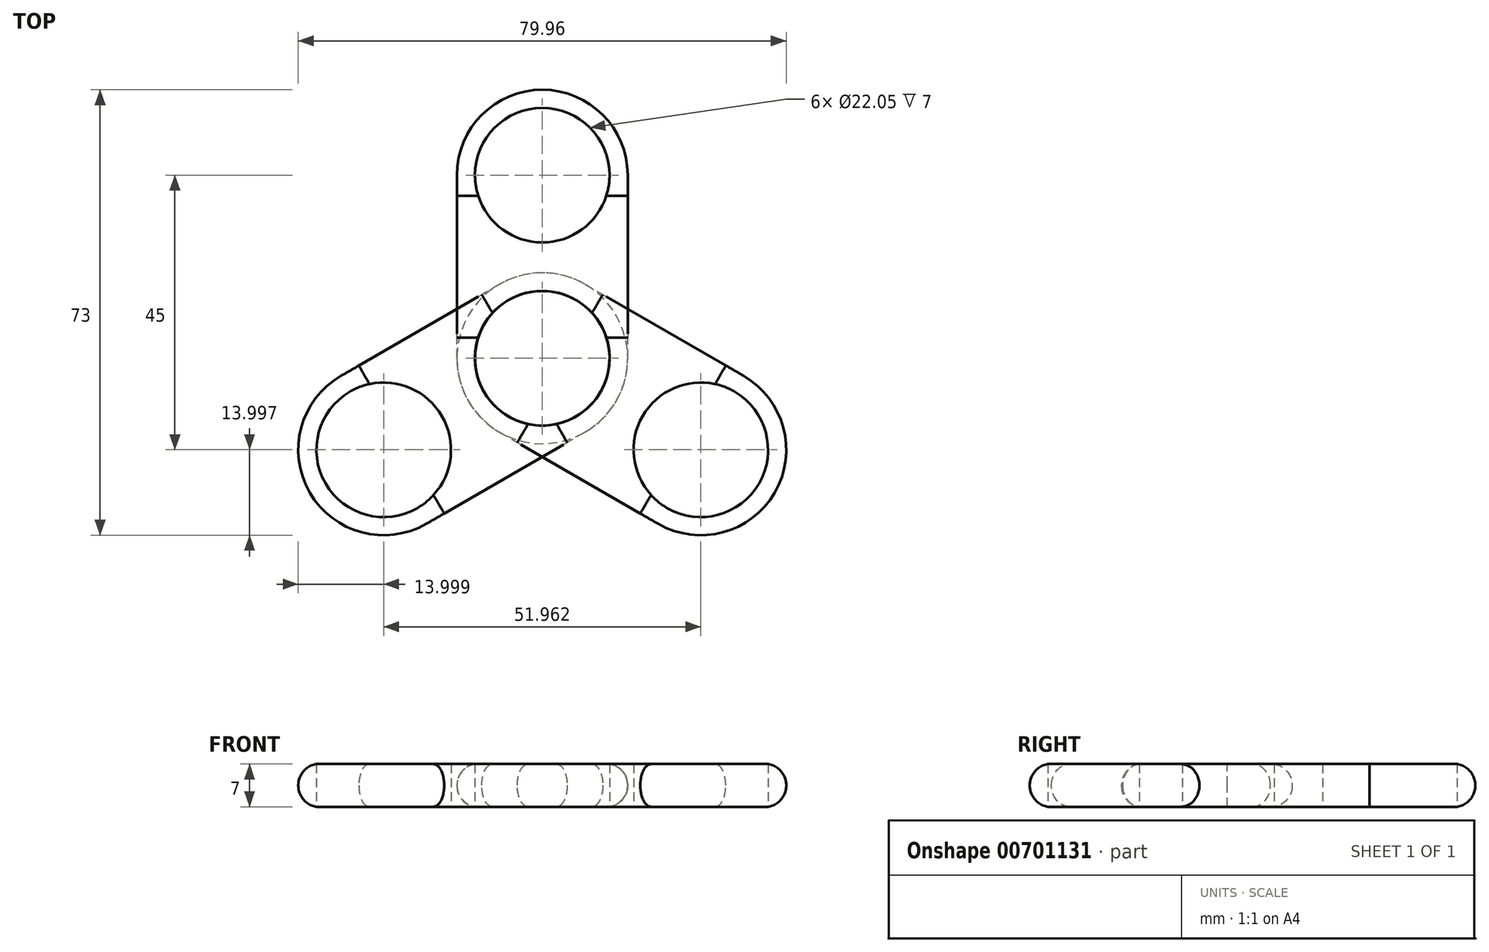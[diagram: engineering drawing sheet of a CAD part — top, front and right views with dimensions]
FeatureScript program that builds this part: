
annotation { "Feature Type Name" : "Feature", "Feature Type Description" : "" }
export const myFeature = defineFeature(function(context is Context, id is Id, definition is map)
    precondition{}
    {
        {
            var Q0;
            Q0=qCreatedBy(makeId("Top.planeOp"),FACE);
            var sketch = newSketch(context, id + "F0", { "sketchPlane" : qUnion([Q0])});
            skArc(sketch, "E0", {"start": v(14, 10.5) * mm, "mid": v(0, 24.5) * mm, "end": v(-14, 10.5) * mm});
            skArc(sketch, "E1", {"start": v(-14, -19.5) * mm, "mid": v(0, -33.5) * mm, "end": v(14, -19.5) * mm});
            skCircle(sketch, "E2", {"center": v(0, 10.5) * mm, "radius": 11.03 * mm});
            skCircle(sketch, "E3", {"center": v(0, -19.5) * mm, "radius": 11.03 * mm});
            skLineSegment(sketch, "E4", {"start": v(-14, -19.5) * mm, "end": v(-14, 10.5) * mm});
            skLineSegment(sketch, "E5", {"start": v(14, -19.5) * mm, "end": v(14, 10.5) * mm});
            skSolve(sketch);
        }
        {
            var Q0;
            Q0=makeQuery(id+"F0.imprint","IMPRINT",FACE,{"disambiguationData":[TD([[makeQuery(id+"F0.imprint","IMPRINT",EDGE,{"derivedFrom":sQuery(id+"F0.wireOp",EDGE,"E0")}),1.0]])]});
            extrude(context, id + "F1", {"entities" : qUnion([Q0]), "depth" : 7 * mm, "offsetDistance" : 25 * mm});
        }
        {
            var Q0;
            Q0=makeQuery(id+"F1.opExtrude","CAP_EDGE",EDGE,{"disambiguationData":[OSD([sQuery(id+"F0.wireOp",EDGE,"E5")])],"isStart":false});
            var Q1;
            Q1=makeQuery(id+"F1.opExtrude","CAP_EDGE",EDGE,{"disambiguationData":[OSD([sQuery(id+"F0.wireOp",EDGE,"E4")])],"isStart":false});
            var Q2;
            Q2=makeQuery(id+"F1.opExtrude","CAP_EDGE",EDGE,{"disambiguationData":[OSD([sQuery(id+"F0.wireOp",EDGE,"E1")])],"isStart":false});
            var Q3;
            Q3=makeQuery(id+"F1.opExtrude","CAP_EDGE",EDGE,{"disambiguationData":[OSD([sQuery(id+"F0.wireOp",EDGE,"E0")])],"isStart":false});
            fillet(context, id + "F2", {"entities" : qUnion([Q0, Q1, Q2, Q3]), "radius" : 3.5 * mm, "tangentPropagation" : true, "allowEdgeOverflow" : false});
        }
        {
            var Q0;
            Q0=makeQuery(id+"F1.opExtrude","CAP_EDGE",EDGE,{"disambiguationData":[OSD([sQuery(id+"F0.wireOp",EDGE,"E5")])],"isStart":true});
            var Q1;
            Q1=makeQuery(id+"F1.opExtrude","CAP_EDGE",EDGE,{"disambiguationData":[OSD([sQuery(id+"F0.wireOp",EDGE,"E4")])],"isStart":true});
            var Q2;
            Q2=makeQuery(id+"F1.opExtrude","CAP_EDGE",EDGE,{"disambiguationData":[OSD([sQuery(id+"F0.wireOp",EDGE,"E0")])],"isStart":true});
            var Q3;
            Q3=makeQuery(id+"F1.opExtrude","CAP_EDGE",EDGE,{"disambiguationData":[OSD([sQuery(id+"F0.wireOp",EDGE,"E1")])],"isStart":true});
            fillet(context, id + "F3", {"entities" : qUnion([Q0, Q1, Q2, Q3]), "radius" : 3.5 * mm, "tangentPropagation" : true, "allowEdgeOverflow" : false});
        }
        {
            var Q0;
            Q0=makeQuery(id+"F1.opExtrude","SWEPT_BODY",BODY,{"disambiguationData":[OSD([sQuery(id+"F0.wireOp",EDGE,"E0"),sQuery(id+"F0.wireOp",EDGE,"E1"),sQuery(id+"F0.wireOp",EDGE,"E2"),sQuery(id+"F0.wireOp",EDGE,"E3"),sQuery(id+"F0.wireOp",EDGE,"E4"),sQuery(id+"F0.wireOp",EDGE,"E5")])]});
            var Q1;
            Q1=makeQuery(id+"F2.opFillet","BLEND_FACE",FACE,{"disambiguationData":[OSD([sQuery(id+"F0.wireOp",EDGE,"E5")]),OD(1.0)]});
            circularPattern(context, id + "F4", {"entities" : qUnion([Q0]), "axis" : qUnion([Q1]), "angle" : 360 * degree, "instanceCount" : 3, "equalSpace" : true});
        }
    });
